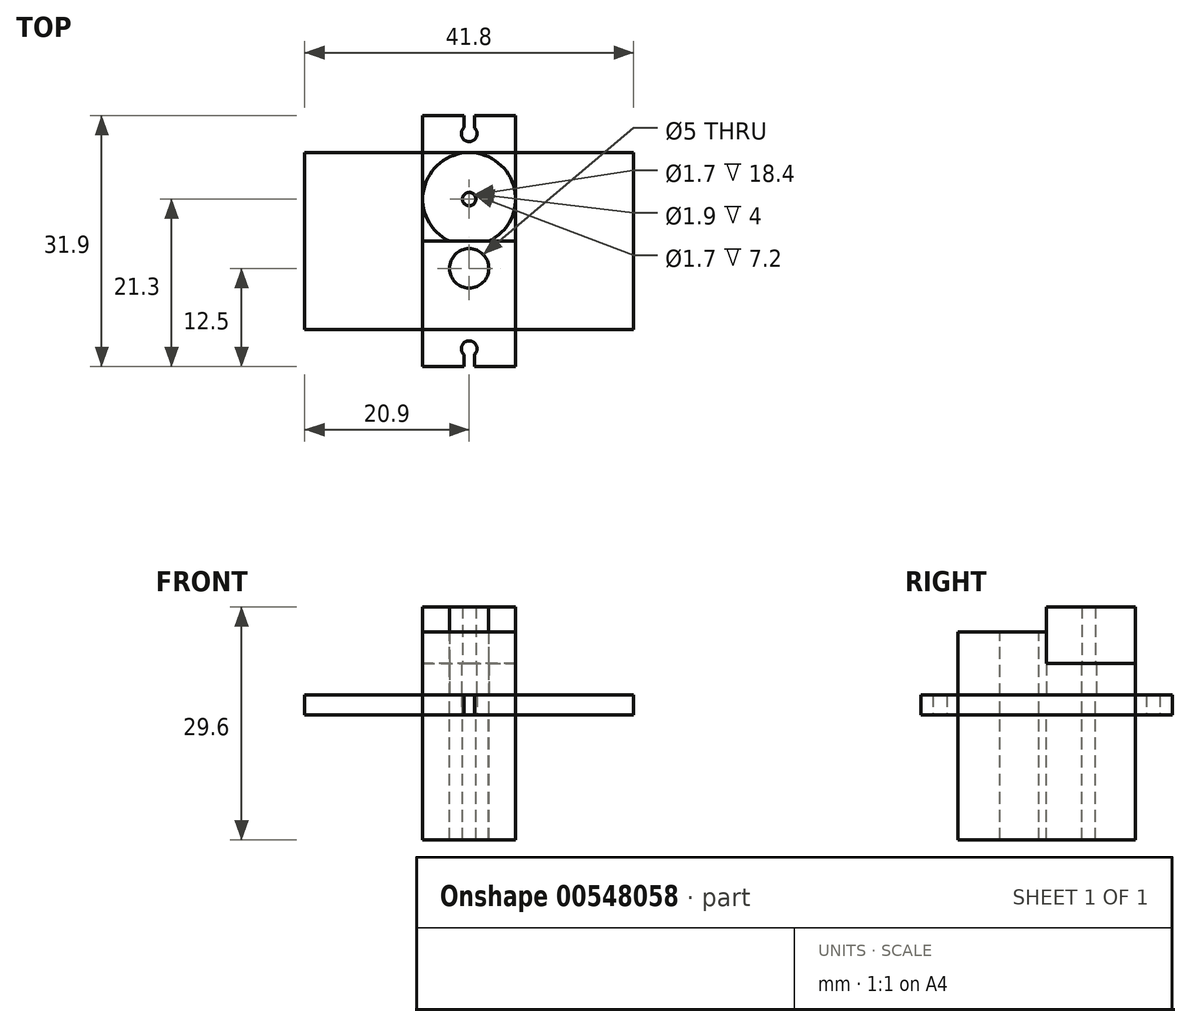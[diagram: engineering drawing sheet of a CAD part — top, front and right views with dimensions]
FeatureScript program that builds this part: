
annotation { "Feature Type Name" : "Feature", "Feature Type Description" : "" }
export const myFeature = defineFeature(function(context is Context, id is Id, definition is map)
    precondition{}
    {
        {
            var Q0;
            Q0=qCreatedBy(makeId("Top.planeOp"),FACE);
            var sketch = newSketch(context, id + "F0", { "sketchPlane" : qUnion([Q0])});
            skLineSegment(sketch, "E0.bottom", {"start": v(0, 0) * mm, "end": v(-11.8, 0) * mm});
            skLineSegment(sketch, "E0.top", {"start": v(0, 31.9) * mm, "end": v(-11.8, 31.9) * mm});
            skLineSegment(sketch, "E0.left", {"start": v(0, 0) * mm, "end": v(0, 31.9) * mm});
            skLineSegment(sketch, "E0.right", {"start": v(-11.8, 0) * mm, "end": v(-11.8, 31.9) * mm});
            skLineSegment(sketch, "E1", {"start": v(-11.8, 27.2) * mm, "end": v(0, 27.2) * mm});
            skLineSegment(sketch, "E2", {"start": v(-11.8, 4.7) * mm, "end": v(0, 4.7) * mm});
            skLineSegment(sketch, "E3", {"start": v(-5.9, 31.9) * mm, "end": v(-5.9, 0) * mm});
            skCircle(sketch, "E4", {"center": v(-5.9, 21.3) * mm, "radius": 5.9 * mm});
            skPoint(sketch, "E4.first.point", {"position": v(-11.8, 21.3) * mm});
            skPoint(sketch, "E4.second.point", {"position": v(0, 21.3) * mm});
            skPoint(sketch, "E4.third.point", {"position": v(-5.9, 27.2) * mm});
            skCircle(sketch, "E5", {"center": v(-5.9, 21.3) * mm, "radius": 2.3 * mm});
            skPoint(sketch, "E6", {"position": v(-6.55, 31.9) * mm});
            skPoint(sketch, "E7", {"position": v(-5.25, 31.9) * mm});
            skPoint(sketch, "E8", {"position": v(-5.9, 29.6) * mm});
            skCircle(sketch, "E9", {"center": v(-5.9, 29.6) * mm, "radius": 1 * mm});
            skLineSegment(sketch, "E10", {"start": v(-6.55, 31.9) * mm, "end": v(-6.55, 30.36) * mm});
            skLineSegment(sketch, "E11", {"start": v(-5.25, 31.9) * mm, "end": v(-5.25, 30.36) * mm});
            skPoint(sketch, "E12", {"position": v(-11.8, 15.95) * mm});
            skPoint(sketch, "E13", {"position": v(0, 15.95) * mm});
            skLineSegment(sketch, "E14", {"start": v(-11.8, 15.95) * mm, "end": v(0, 15.95) * mm});
            skPoint(sketch, "E15.MirrorP", {"position": v(-5.9, 2.3) * mm});
            skLineSegment(sketch, "E16.MirrorCS", {"start": v(-6.55, 0) * mm, "end": v(-6.55, 1.54) * mm});
            skLineSegment(sketch, "E17.MirrorCS", {"start": v(-5.25, 0) * mm, "end": v(-5.25, 1.54) * mm});
            skCircle(sketch, "E18.MirrorC", {"center": v(-5.9, 2.3) * mm, "radius": 1 * mm});
            skCircle(sketch, "E19", {"center": v(-5.9, 21.3) * mm, "radius": 0.85 * mm});
            skPoint(sketch, "E20", {"position": v(-5.9, 12.5) * mm});
            skCircle(sketch, "E21", {"center": v(-5.9, 12.5) * mm, "radius": 2.5 * mm});
            skLineSegment(sketch, "E22", {"start": v(-3.4, 12.5) * mm, "end": v(-3.4, 15.96) * mm});
            skLineSegment(sketch, "E23", {"start": v(-8.4, 12.5) * mm, "end": v(-8.4, 15.96) * mm});
            skSolve(sketch);
        }
        {
            var Q0;
            {var subQ0=sQuery(id+"F0.wireOp",EDGE,"E1");var subQ1=sQuery(id+"F0.wireOp",EDGE,"E0.left");var subQ2=makeQuery(id+"F0.imprint","INTERSECT",VERTEX,{"derivedFrom":[subQ1,subQ0]});Q0=makeQuery(id+"F0.imprint","IMPRINT",FACE,{"disambiguationData":[TD([[makeQuery(id+"F0.imprint","IMPRINT",EDGE,{"disambiguationData":[TD([[subQ2,1.0]])],"derivedFrom":subQ1}),1.0]])]});}
            var Q1;
            {var subQ0=sQuery(id+"F0.wireOp",EDGE,"E1");var subQ1=sQuery(id+"F0.wireOp",EDGE,"E0.right");var subQ2=makeQuery(id+"F0.imprint","INTERSECT",VERTEX,{"derivedFrom":[subQ1,subQ0]});Q1=makeQuery(id+"F0.imprint","IMPRINT",FACE,{"disambiguationData":[TD([[makeQuery(id+"F0.imprint","IMPRINT",EDGE,{"disambiguationData":[TD([[subQ2,1.0]])],"derivedFrom":subQ1}),-1.0]])]});}
            var Q2;
            {var subQ0=sQuery(id+"F0.wireOp",EDGE,"E14");var subQ1=sQuery(id+"F0.wireOp",EDGE,"E0.left");var subQ2=makeQuery(id+"F0.imprint","INTERSECT",VERTEX,{"derivedFrom":[subQ1,subQ0]});Q2=makeQuery(id+"F0.imprint","IMPRINT",FACE,{"disambiguationData":[TD([[makeQuery(id+"F0.imprint","IMPRINT",EDGE,{"disambiguationData":[TD([[subQ2,-1.0]])],"derivedFrom":subQ1}),1.0]])]});}
            var Q3;
            {var subQ0=sQuery(id+"F0.wireOp",EDGE,"E14");var subQ1=sQuery(id+"F0.wireOp",EDGE,"E0.right");var subQ2=makeQuery(id+"F0.imprint","INTERSECT",VERTEX,{"derivedFrom":[subQ1,subQ0]});Q3=makeQuery(id+"F0.imprint","IMPRINT",FACE,{"disambiguationData":[TD([[makeQuery(id+"F0.imprint","IMPRINT",EDGE,{"disambiguationData":[TD([[subQ2,-1.0]])],"derivedFrom":subQ1}),-1.0]])]});}
            var Q4;
            {var subQ1=sQuery(id+"F0.wireOp",EDGE,"E0.left");var subQ6=sQuery(id+"F0.wireOp",EDGE,"E2");var subQ10=makeQuery(id+"F0.imprint","INTERSECT",VERTEX,{"derivedFrom":[subQ1,subQ6]});Q4=makeQuery(id+"F0.imprint","IMPRINT",FACE,{"disambiguationData":[TD([[makeQuery(id+"F0.imprint","IMPRINT",EDGE,{"disambiguationData":[TD([[subQ10,-1.0]])],"derivedFrom":subQ1}),1.0]])]});}
            var Q5;
            {var subQ1=sQuery(id+"F0.wireOp",EDGE,"E0.right");var subQ5=sQuery(id+"F0.wireOp",EDGE,"E2");var subQ6=makeQuery(id+"F0.imprint","INTERSECT",VERTEX,{"derivedFrom":[subQ1,subQ5]});Q5=makeQuery(id+"F0.imprint","IMPRINT",FACE,{"disambiguationData":[TD([[makeQuery(id+"F0.imprint","IMPRINT",EDGE,{"disambiguationData":[TD([[subQ6,-1.0]])],"derivedFrom":subQ1}),-1.0]])]});}
            var Q6;
            {var subQ5=sQuery(id+"F0.wireOp",EDGE,"E3");var subQ7=sQuery(id+"F0.wireOp",EDGE,"E5");var subQ8=makeQuery(id+"F0.imprint","INTERSECT",VERTEX,{"disambiguationData":[OD(1.0)],"derivedFrom":[subQ5,subQ7]});Q6=makeQuery(id+"F0.imprint","IMPRINT",FACE,{"disambiguationData":[TD([[makeQuery(id+"F0.imprint","IMPRINT",EDGE,{"disambiguationData":[TD([[subQ8,-1.0]])],"derivedFrom":subQ5}),1.0]])]});}
            var Q7;
            {var subQ0=sQuery(id+"F0.wireOp",EDGE,"E5");var subQ1=sQuery(id+"F0.wireOp",EDGE,"E3");var subQ2=makeQuery(id+"F0.imprint","INTERSECT",VERTEX,{"disambiguationData":[OD(0.0)],"derivedFrom":[subQ1,subQ0]});Q7=makeQuery(id+"F0.imprint","IMPRINT",FACE,{"disambiguationData":[TD([[makeQuery(id+"F0.imprint","IMPRINT",EDGE,{"disambiguationData":[TD([[subQ2,-1.0]])],"derivedFrom":subQ1}),1.0]])]});}
            var Q8;
            {var subQ0=sQuery(id+"F0.wireOp",EDGE,"E5");var subQ1=sQuery(id+"F0.wireOp",EDGE,"E3");var subQ2=makeQuery(id+"F0.imprint","INTERSECT",VERTEX,{"disambiguationData":[OD(0.0)],"derivedFrom":[subQ1,subQ0]});Q8=makeQuery(id+"F0.imprint","IMPRINT",FACE,{"disambiguationData":[TD([[makeQuery(id+"F0.imprint","IMPRINT",EDGE,{"disambiguationData":[TD([[subQ2,-1.0]])],"derivedFrom":subQ1}),-1.0]])]});}
            var Q9;
            {var subQ0=sQuery(id+"F0.wireOp",EDGE,"E19");var subQ1=sQuery(id+"F0.wireOp",EDGE,"E3");var subQ2=makeQuery(id+"F0.imprint","INTERSECT",VERTEX,{"disambiguationData":[OD(0.0)],"derivedFrom":[subQ1,subQ0]});Q9=makeQuery(id+"F0.imprint","IMPRINT",FACE,{"disambiguationData":[TD([[makeQuery(id+"F0.imprint","IMPRINT",EDGE,{"disambiguationData":[TD([[subQ2,-1.0]])],"derivedFrom":subQ1}),1.0]])]});}
            var Q10;
            {var subQ0=sQuery(id+"F0.wireOp",EDGE,"E19");var subQ1=sQuery(id+"F0.wireOp",EDGE,"E3");var subQ2=makeQuery(id+"F0.imprint","INTERSECT",VERTEX,{"disambiguationData":[OD(0.0)],"derivedFrom":[subQ1,subQ0]});Q10=makeQuery(id+"F0.imprint","IMPRINT",FACE,{"disambiguationData":[TD([[makeQuery(id+"F0.imprint","IMPRINT",EDGE,{"disambiguationData":[TD([[subQ2,-1.0]])],"derivedFrom":subQ1}),-1.0]])]});}
            var Q11;
            {var subQ0=sQuery(id+"F0.wireOp",EDGE,"E21");var subQ1=sQuery(id+"F0.wireOp",EDGE,"E3");var subQ2=makeQuery(id+"F0.imprint","INTERSECT",VERTEX,{"disambiguationData":[OD(0.0)],"derivedFrom":[subQ1,subQ0]});Q11=makeQuery(id+"F0.imprint","IMPRINT",FACE,{"disambiguationData":[TD([[makeQuery(id+"F0.imprint","IMPRINT",EDGE,{"disambiguationData":[TD([[subQ2,-1.0]])],"derivedFrom":subQ1}),-1.0]])]});}
            var Q12;
            {var subQ0=sQuery(id+"F0.wireOp",EDGE,"E21");var subQ1=sQuery(id+"F0.wireOp",EDGE,"E3");var subQ2=makeQuery(id+"F0.imprint","INTERSECT",VERTEX,{"disambiguationData":[OD(0.0)],"derivedFrom":[subQ1,subQ0]});Q12=makeQuery(id+"F0.imprint","IMPRINT",FACE,{"disambiguationData":[TD([[makeQuery(id+"F0.imprint","IMPRINT",EDGE,{"disambiguationData":[TD([[subQ2,-1.0]])],"derivedFrom":subQ1}),1.0]])]});}
            var Q13;
            {var subQ3=sQuery(id+"F0.wireOp",EDGE,"E3");var subQ6=sQuery(id+"F0.wireOp",EDGE,"E4");var subQ9=makeQuery(id+"F0.imprint","INTERSECT",VERTEX,{"derivedFrom":[subQ3,subQ6]});Q13=makeQuery(id+"F0.imprint","IMPRINT",FACE,{"disambiguationData":[TD([[makeQuery(id+"F0.imprint","IMPRINT",EDGE,{"disambiguationData":[TD([[subQ9,-1.0]])],"derivedFrom":subQ3}),1.0]])]});}
            var Q14;
            {var subQ0=sQuery(id+"F0.wireOp",EDGE,"E14");var subQ1=sQuery(id+"F0.wireOp",EDGE,"E3");var subQ2=makeQuery(id+"F0.imprint","INTERSECT",VERTEX,{"derivedFrom":[subQ1,subQ0]});Q14=makeQuery(id+"F0.imprint","IMPRINT",FACE,{"disambiguationData":[TD([[makeQuery(id+"F0.imprint","IMPRINT",EDGE,{"disambiguationData":[TD([[subQ2,-1.0]])],"derivedFrom":subQ1}),1.0]])]});}
            var Q15;
            {var subQ3=sQuery(id+"F0.wireOp",EDGE,"E3");var subQ6=sQuery(id+"F0.wireOp",EDGE,"E4");var subQ9=makeQuery(id+"F0.imprint","INTERSECT",VERTEX,{"derivedFrom":[subQ3,subQ6]});Q15=makeQuery(id+"F0.imprint","IMPRINT",FACE,{"disambiguationData":[TD([[makeQuery(id+"F0.imprint","IMPRINT",EDGE,{"disambiguationData":[TD([[subQ9,-1.0]])],"derivedFrom":subQ3}),-1.0]])]});}
            var Q16;
            {var subQ2=sQuery(id+"F0.wireOp",EDGE,"E3");var subQ5=sQuery(id+"F0.wireOp",EDGE,"E5");var subQ6=makeQuery(id+"F0.imprint","INTERSECT",VERTEX,{"disambiguationData":[OD(1.0)],"derivedFrom":[subQ2,subQ5]});Q16=makeQuery(id+"F0.imprint","IMPRINT",FACE,{"disambiguationData":[TD([[makeQuery(id+"F0.imprint","IMPRINT",EDGE,{"disambiguationData":[TD([[subQ6,-1.0]])],"derivedFrom":subQ2}),-1.0]])]});}
            var Q17;
            {var subQ0=sQuery(id+"F0.wireOp",EDGE,"E14");var subQ1=sQuery(id+"F0.wireOp",EDGE,"E3");var subQ2=makeQuery(id+"F0.imprint","INTERSECT",VERTEX,{"derivedFrom":[subQ1,subQ0]});Q17=makeQuery(id+"F0.imprint","IMPRINT",FACE,{"disambiguationData":[TD([[makeQuery(id+"F0.imprint","IMPRINT",EDGE,{"disambiguationData":[TD([[subQ2,-1.0]])],"derivedFrom":subQ1}),-1.0]])]});}
            extrude(context, id + "F1", {"entities" : qUnion([Q0, Q1, Q2, Q3, Q4, Q5, Q6, Q7, Q8, Q9, Q10, Q11, Q12, Q13, Q14, Q15, Q16, Q17]), "oppositeDirection" : true, "depth" : 15.9 * mm});
        }
        {
            var Q0;
            {var subQ0=sQuery(id+"F0.wireOp",EDGE,"E1");var subQ1=sQuery(id+"F0.wireOp",EDGE,"E0.left");var subQ2=makeQuery(id+"F0.imprint","INTERSECT",VERTEX,{"derivedFrom":[subQ1,subQ0]});Q0=makeQuery(id+"F0.imprint","IMPRINT",FACE,{"disambiguationData":[TD([[makeQuery(id+"F0.imprint","IMPRINT",EDGE,{"disambiguationData":[TD([[subQ2,1.0]])],"derivedFrom":subQ1}),1.0]])]});}
            var Q1;
            {var subQ0=sQuery(id+"F0.wireOp",EDGE,"E1");var subQ1=sQuery(id+"F0.wireOp",EDGE,"E0.right");var subQ2=makeQuery(id+"F0.imprint","INTERSECT",VERTEX,{"derivedFrom":[subQ1,subQ0]});Q1=makeQuery(id+"F0.imprint","IMPRINT",FACE,{"disambiguationData":[TD([[makeQuery(id+"F0.imprint","IMPRINT",EDGE,{"disambiguationData":[TD([[subQ2,1.0]])],"derivedFrom":subQ1}),-1.0]])]});}
            var Q2;
            {var subQ0=sQuery(id+"F0.wireOp",EDGE,"E14");var subQ1=sQuery(id+"F0.wireOp",EDGE,"E0.left");var subQ2=makeQuery(id+"F0.imprint","INTERSECT",VERTEX,{"derivedFrom":[subQ1,subQ0]});Q2=makeQuery(id+"F0.imprint","IMPRINT",FACE,{"disambiguationData":[TD([[makeQuery(id+"F0.imprint","IMPRINT",EDGE,{"disambiguationData":[TD([[subQ2,-1.0]])],"derivedFrom":subQ1}),1.0]])]});}
            var Q3;
            {var subQ0=sQuery(id+"F0.wireOp",EDGE,"E14");var subQ1=sQuery(id+"F0.wireOp",EDGE,"E0.right");var subQ2=makeQuery(id+"F0.imprint","INTERSECT",VERTEX,{"derivedFrom":[subQ1,subQ0]});Q3=makeQuery(id+"F0.imprint","IMPRINT",FACE,{"disambiguationData":[TD([[makeQuery(id+"F0.imprint","IMPRINT",EDGE,{"disambiguationData":[TD([[subQ2,-1.0]])],"derivedFrom":subQ1}),-1.0]])]});}
            var Q4;
            {var subQ9=sQuery(id+"F0.wireOp",EDGE,"E17.MirrorCS");Q4=makeQuery(id+"F0.imprint","IMPRINT",FACE,{"disambiguationData":[TD([[makeQuery(id+"F0.imprint","IMPRINT",EDGE,{"derivedFrom":subQ9}),-1.0]])]});}
            var Q5;
            {var subQ9=sQuery(id+"F0.wireOp",EDGE,"E16.MirrorCS");Q5=makeQuery(id+"F0.imprint","IMPRINT",FACE,{"disambiguationData":[TD([[makeQuery(id+"F0.imprint","IMPRINT",EDGE,{"derivedFrom":subQ9}),1.0]])]});}
            var Q6;
            {var subQ9=sQuery(id+"F0.wireOp",EDGE,"E11");Q6=makeQuery(id+"F0.imprint","IMPRINT",FACE,{"disambiguationData":[TD([[makeQuery(id+"F0.imprint","IMPRINT",EDGE,{"derivedFrom":subQ9}),1.0]])]});}
            var Q7;
            {var subQ9=sQuery(id+"F0.wireOp",EDGE,"E10");Q7=makeQuery(id+"F0.imprint","IMPRINT",FACE,{"disambiguationData":[TD([[makeQuery(id+"F0.imprint","IMPRINT",EDGE,{"derivedFrom":subQ9}),-1.0]])]});}
            var Q8;
            {var subQ1=sQuery(id+"F0.wireOp",EDGE,"E0.left");var subQ6=sQuery(id+"F0.wireOp",EDGE,"E2");var subQ10=makeQuery(id+"F0.imprint","INTERSECT",VERTEX,{"derivedFrom":[subQ1,subQ6]});Q8=makeQuery(id+"F0.imprint","IMPRINT",FACE,{"disambiguationData":[TD([[makeQuery(id+"F0.imprint","IMPRINT",EDGE,{"disambiguationData":[TD([[subQ10,-1.0]])],"derivedFrom":subQ1}),1.0]])]});}
            var Q9;
            {var subQ1=sQuery(id+"F0.wireOp",EDGE,"E0.right");var subQ5=sQuery(id+"F0.wireOp",EDGE,"E2");var subQ6=makeQuery(id+"F0.imprint","INTERSECT",VERTEX,{"derivedFrom":[subQ1,subQ5]});Q9=makeQuery(id+"F0.imprint","IMPRINT",FACE,{"disambiguationData":[TD([[makeQuery(id+"F0.imprint","IMPRINT",EDGE,{"disambiguationData":[TD([[subQ6,-1.0]])],"derivedFrom":subQ1}),-1.0]])]});}
            var Q10;
            {var subQ5=sQuery(id+"F0.wireOp",EDGE,"E3");var subQ7=sQuery(id+"F0.wireOp",EDGE,"E5");var subQ8=makeQuery(id+"F0.imprint","INTERSECT",VERTEX,{"disambiguationData":[OD(1.0)],"derivedFrom":[subQ5,subQ7]});Q10=makeQuery(id+"F0.imprint","IMPRINT",FACE,{"disambiguationData":[TD([[makeQuery(id+"F0.imprint","IMPRINT",EDGE,{"disambiguationData":[TD([[subQ8,-1.0]])],"derivedFrom":subQ5}),1.0]])]});}
            var Q11;
            {var subQ2=sQuery(id+"F0.wireOp",EDGE,"E3");var subQ5=sQuery(id+"F0.wireOp",EDGE,"E5");var subQ6=makeQuery(id+"F0.imprint","INTERSECT",VERTEX,{"disambiguationData":[OD(1.0)],"derivedFrom":[subQ2,subQ5]});Q11=makeQuery(id+"F0.imprint","IMPRINT",FACE,{"disambiguationData":[TD([[makeQuery(id+"F0.imprint","IMPRINT",EDGE,{"disambiguationData":[TD([[subQ6,-1.0]])],"derivedFrom":subQ2}),-1.0]])]});}
            var Q12;
            {var subQ0=sQuery(id+"F0.wireOp",EDGE,"E14");var subQ1=sQuery(id+"F0.wireOp",EDGE,"E3");var subQ2=makeQuery(id+"F0.imprint","INTERSECT",VERTEX,{"derivedFrom":[subQ1,subQ0]});Q12=makeQuery(id+"F0.imprint","IMPRINT",FACE,{"disambiguationData":[TD([[makeQuery(id+"F0.imprint","IMPRINT",EDGE,{"disambiguationData":[TD([[subQ2,-1.0]])],"derivedFrom":subQ1}),1.0]])]});}
            var Q13;
            {var subQ0=sQuery(id+"F0.wireOp",EDGE,"E14");var subQ1=sQuery(id+"F0.wireOp",EDGE,"E3");var subQ2=makeQuery(id+"F0.imprint","INTERSECT",VERTEX,{"derivedFrom":[subQ1,subQ0]});Q13=makeQuery(id+"F0.imprint","IMPRINT",FACE,{"disambiguationData":[TD([[makeQuery(id+"F0.imprint","IMPRINT",EDGE,{"disambiguationData":[TD([[subQ2,-1.0]])],"derivedFrom":subQ1}),-1.0]])]});}
            var Q14;
            {var subQ0=sQuery(id+"F0.wireOp",EDGE,"E21");var subQ1=sQuery(id+"F0.wireOp",EDGE,"E3");var subQ2=makeQuery(id+"F0.imprint","INTERSECT",VERTEX,{"disambiguationData":[OD(0.0)],"derivedFrom":[subQ1,subQ0]});Q14=makeQuery(id+"F0.imprint","IMPRINT",FACE,{"disambiguationData":[TD([[makeQuery(id+"F0.imprint","IMPRINT",EDGE,{"disambiguationData":[TD([[subQ2,-1.0]])],"derivedFrom":subQ1}),1.0]])]});}
            var Q15;
            {var subQ0=sQuery(id+"F0.wireOp",EDGE,"E5");var subQ1=sQuery(id+"F0.wireOp",EDGE,"E3");var subQ2=makeQuery(id+"F0.imprint","INTERSECT",VERTEX,{"disambiguationData":[OD(0.0)],"derivedFrom":[subQ1,subQ0]});Q15=makeQuery(id+"F0.imprint","IMPRINT",FACE,{"disambiguationData":[TD([[makeQuery(id+"F0.imprint","IMPRINT",EDGE,{"disambiguationData":[TD([[subQ2,-1.0]])],"derivedFrom":subQ1}),-1.0]])]});}
            var Q16;
            {var subQ3=sQuery(id+"F0.wireOp",EDGE,"E3");var subQ6=sQuery(id+"F0.wireOp",EDGE,"E4");var subQ9=makeQuery(id+"F0.imprint","INTERSECT",VERTEX,{"derivedFrom":[subQ3,subQ6]});Q16=makeQuery(id+"F0.imprint","IMPRINT",FACE,{"disambiguationData":[TD([[makeQuery(id+"F0.imprint","IMPRINT",EDGE,{"disambiguationData":[TD([[subQ9,-1.0]])],"derivedFrom":subQ3}),1.0]])]});}
            var Q17;
            {var subQ0=sQuery(id+"F0.wireOp",EDGE,"E5");var subQ1=sQuery(id+"F0.wireOp",EDGE,"E3");var subQ2=makeQuery(id+"F0.imprint","INTERSECT",VERTEX,{"disambiguationData":[OD(0.0)],"derivedFrom":[subQ1,subQ0]});Q17=makeQuery(id+"F0.imprint","IMPRINT",FACE,{"disambiguationData":[TD([[makeQuery(id+"F0.imprint","IMPRINT",EDGE,{"disambiguationData":[TD([[subQ2,-1.0]])],"derivedFrom":subQ1}),1.0]])]});}
            var Q18;
            {var subQ0=sQuery(id+"F0.wireOp",EDGE,"E21");var subQ1=sQuery(id+"F0.wireOp",EDGE,"E3");var subQ2=makeQuery(id+"F0.imprint","INTERSECT",VERTEX,{"disambiguationData":[OD(0.0)],"derivedFrom":[subQ1,subQ0]});Q18=makeQuery(id+"F0.imprint","IMPRINT",FACE,{"disambiguationData":[TD([[makeQuery(id+"F0.imprint","IMPRINT",EDGE,{"disambiguationData":[TD([[subQ2,-1.0]])],"derivedFrom":subQ1}),-1.0]])]});}
            var Q19;
            {var subQ3=sQuery(id+"F0.wireOp",EDGE,"E3");var subQ6=sQuery(id+"F0.wireOp",EDGE,"E4");var subQ9=makeQuery(id+"F0.imprint","INTERSECT",VERTEX,{"derivedFrom":[subQ3,subQ6]});Q19=makeQuery(id+"F0.imprint","IMPRINT",FACE,{"disambiguationData":[TD([[makeQuery(id+"F0.imprint","IMPRINT",EDGE,{"disambiguationData":[TD([[subQ9,-1.0]])],"derivedFrom":subQ3}),-1.0]])]});}
            var Q20;
            {var subQ0=sQuery(id+"F0.wireOp",EDGE,"E23");var subQ1=sQuery(id+"F0.wireOp",EDGE,"E4");var subQ2=makeQuery(id+"F0.imprint","INTERSECT",VERTEX,{"derivedFrom":[subQ1,subQ0]});Q20=makeQuery(id+"F0.imprint","IMPRINT",FACE,{"disambiguationData":[TD([[makeQuery(id+"F0.imprint","IMPRINT",EDGE,{"disambiguationData":[TD([[subQ2,-1.0]])],"derivedFrom":subQ1}),-1.0]])]});}
            var Q21;
            {var subQ0=sQuery(id+"F0.wireOp",EDGE,"E22");var subQ1=sQuery(id+"F0.wireOp",EDGE,"E4");var subQ2=makeQuery(id+"F0.imprint","INTERSECT",VERTEX,{"derivedFrom":[subQ1,subQ0]});Q21=makeQuery(id+"F0.imprint","IMPRINT",FACE,{"disambiguationData":[TD([[makeQuery(id+"F0.imprint","IMPRINT",EDGE,{"disambiguationData":[TD([[subQ2,1.0]])],"derivedFrom":subQ1}),-1.0]])]});}
            var Q22;
            {var subQ0=sQuery(id+"F0.wireOp",EDGE,"E19");var subQ1=sQuery(id+"F0.wireOp",EDGE,"E3");var subQ2=makeQuery(id+"F0.imprint","INTERSECT",VERTEX,{"disambiguationData":[OD(0.0)],"derivedFrom":[subQ1,subQ0]});Q22=makeQuery(id+"F0.imprint","IMPRINT",FACE,{"disambiguationData":[TD([[makeQuery(id+"F0.imprint","IMPRINT",EDGE,{"disambiguationData":[TD([[subQ2,-1.0]])],"derivedFrom":subQ1}),1.0]])]});}
            var Q23;
            {var subQ0=sQuery(id+"F0.wireOp",EDGE,"E19");var subQ1=sQuery(id+"F0.wireOp",EDGE,"E3");var subQ2=makeQuery(id+"F0.imprint","INTERSECT",VERTEX,{"disambiguationData":[OD(0.0)],"derivedFrom":[subQ1,subQ0]});Q23=makeQuery(id+"F0.imprint","IMPRINT",FACE,{"disambiguationData":[TD([[makeQuery(id+"F0.imprint","IMPRINT",EDGE,{"disambiguationData":[TD([[subQ2,-1.0]])],"derivedFrom":subQ1}),-1.0]])]});}
            extrude(context, id + "F2", {"entities" : qUnion([Q0, Q1, Q2, Q3, Q4, Q5, Q6, Q7, Q8, Q9, Q10, Q11, Q12, Q13, Q14, Q15, Q16, Q17, Q18, Q19, Q20, Q21, Q22, Q23]), "operationType" : NewBodyOperationType.ADD, "depth" : 2.5 * mm});
        }
        {
            var Q0;
            Q0=makeQuery(id+"F2.opExtrude","CAP_EDGE",EDGE,{"disambiguationData":[OSD([sQuery(id+"F0.wireOp",EDGE,"E0.right")])],"isStart":false});
            cPlane(context, id + "F3", {"entities" : qUnion([Q0]), "cplaneType" : CPlaneType.LINE_ANGLE, "offset" : 25 * mm, "angle" : 0 * degree, "width" : 150 * mm, "height" : 150 * mm});
        }
        {
            var Q0;
            Q0=qCreatedBy(id+"F3.planeOp",FACE);
            var sketch = newSketch(context, id + "F4", { "sketchPlane" : qUnion([Q0])});
            skLineSegment(sketch, "E24.bottom", {"start": v(0, 0) * mm, "end": v(-11.8, 0) * mm});
            skLineSegment(sketch, "E24.top", {"start": v(0, 31.9) * mm, "end": v(-11.8, 31.9) * mm});
            skLineSegment(sketch, "E24.left", {"start": v(0, 0) * mm, "end": v(0, 31.9) * mm});
            skLineSegment(sketch, "E24.right", {"start": v(-11.8, 0) * mm, "end": v(-11.8, 31.9) * mm});
            skLineSegment(sketch, "E25", {"start": v(-11.8, 27.2) * mm, "end": v(0, 27.2) * mm});
            skLineSegment(sketch, "E26", {"start": v(-11.8, 4.7) * mm, "end": v(0, 4.7) * mm});
            skLineSegment(sketch, "E27", {"start": v(-5.9, 31.9) * mm, "end": v(-5.9, 0) * mm});
            skCircle(sketch, "E28", {"center": v(-5.9, 21.3) * mm, "radius": 5.9 * mm});
            skPoint(sketch, "E28.first.point", {"position": v(-11.8, 21.3) * mm});
            skPoint(sketch, "E28.second.point", {"position": v(0, 21.3) * mm});
            skPoint(sketch, "E28.third.point", {"position": v(-5.9, 27.2) * mm});
            skCircle(sketch, "E29", {"center": v(-5.9, 21.3) * mm, "radius": 2.3 * mm});
            skPoint(sketch, "E30", {"position": v(-6.55, 31.9) * mm});
            skPoint(sketch, "E31", {"position": v(-5.25, 31.9) * mm});
            skPoint(sketch, "E32", {"position": v(-5.9, 29.6) * mm});
            skCircle(sketch, "E33", {"center": v(-5.9, 29.6) * mm, "radius": 1 * mm});
            skLineSegment(sketch, "E34", {"start": v(-6.55, 31.9) * mm, "end": v(-6.55, 30.36) * mm});
            skLineSegment(sketch, "E35", {"start": v(-5.25, 31.9) * mm, "end": v(-5.25, 30.36) * mm});
            skPoint(sketch, "E36", {"position": v(-11.8, 15.95) * mm});
            skPoint(sketch, "E37", {"position": v(0, 15.95) * mm});
            skLineSegment(sketch, "E38", {"start": v(-11.8, 15.95) * mm, "end": v(0, 15.95) * mm});
            skPoint(sketch, "E39.MirrorP", {"position": v(-5.9, 2.3) * mm});
            skLineSegment(sketch, "E40.MirrorCS", {"start": v(-6.55, 0) * mm, "end": v(-6.55, 1.54) * mm});
            skLineSegment(sketch, "E41.MirrorCS", {"start": v(-5.25, 0) * mm, "end": v(-5.25, 1.54) * mm});
            skCircle(sketch, "E42.MirrorC", {"center": v(-5.9, 2.3) * mm, "radius": 1 * mm});
            skCircle(sketch, "E43", {"center": v(-5.9, 21.3) * mm, "radius": 0.95 * mm});
            skPoint(sketch, "E44", {"position": v(-5.9, 12.5) * mm});
            skCircle(sketch, "E45", {"center": v(-5.9, 12.5) * mm, "radius": 2.5 * mm});
            skLineSegment(sketch, "E46", {"start": v(-3.4, 12.5) * mm, "end": v(-3.4, 15.96) * mm});
            skLineSegment(sketch, "E47", {"start": v(-8.4, 12.5) * mm, "end": v(-8.4, 15.96) * mm});
            skSolve(sketch);
        }
        {
            var Q0;
            {var subQ0=sQuery(id+"F4.wireOp",EDGE,"E25");var subQ1=sQuery(id+"F4.wireOp",EDGE,"E24.left");var subQ2=makeQuery(id+"F4.imprint","INTERSECT",VERTEX,{"derivedFrom":[subQ1,subQ0]});Q0=makeQuery(id+"F4.imprint","IMPRINT",FACE,{"disambiguationData":[TD([[makeQuery(id+"F4.imprint","IMPRINT",EDGE,{"disambiguationData":[TD([[subQ2,1.0]])],"derivedFrom":subQ1}),1.0]])]});}
            var Q1;
            {var subQ0=sQuery(id+"F4.wireOp",EDGE,"E25");var subQ1=sQuery(id+"F4.wireOp",EDGE,"E24.right");var subQ2=makeQuery(id+"F4.imprint","INTERSECT",VERTEX,{"derivedFrom":[subQ1,subQ0]});Q1=makeQuery(id+"F4.imprint","IMPRINT",FACE,{"disambiguationData":[TD([[makeQuery(id+"F4.imprint","IMPRINT",EDGE,{"disambiguationData":[TD([[subQ2,1.0]])],"derivedFrom":subQ1}),-1.0]])]});}
            var Q2;
            {var subQ0=sQuery(id+"F4.wireOp",EDGE,"E38");var subQ1=sQuery(id+"F4.wireOp",EDGE,"E24.left");var subQ2=makeQuery(id+"F4.imprint","INTERSECT",VERTEX,{"derivedFrom":[subQ1,subQ0]});Q2=makeQuery(id+"F4.imprint","IMPRINT",FACE,{"disambiguationData":[TD([[makeQuery(id+"F4.imprint","IMPRINT",EDGE,{"disambiguationData":[TD([[subQ2,-1.0]])],"derivedFrom":subQ1}),1.0]])]});}
            var Q3;
            {var subQ0=sQuery(id+"F4.wireOp",EDGE,"E38");var subQ1=sQuery(id+"F4.wireOp",EDGE,"E24.right");var subQ2=makeQuery(id+"F4.imprint","INTERSECT",VERTEX,{"derivedFrom":[subQ1,subQ0]});Q3=makeQuery(id+"F4.imprint","IMPRINT",FACE,{"disambiguationData":[TD([[makeQuery(id+"F4.imprint","IMPRINT",EDGE,{"disambiguationData":[TD([[subQ2,-1.0]])],"derivedFrom":subQ1}),-1.0]])]});}
            var Q4;
            {var subQ1=sQuery(id+"F4.wireOp",EDGE,"E24.left");var subQ6=sQuery(id+"F4.wireOp",EDGE,"E26");var subQ10=makeQuery(id+"F4.imprint","INTERSECT",VERTEX,{"derivedFrom":[subQ1,subQ6]});Q4=makeQuery(id+"F4.imprint","IMPRINT",FACE,{"disambiguationData":[TD([[makeQuery(id+"F4.imprint","IMPRINT",EDGE,{"disambiguationData":[TD([[subQ10,-1.0]])],"derivedFrom":subQ1}),1.0]])]});}
            var Q5;
            {var subQ1=sQuery(id+"F4.wireOp",EDGE,"E24.right");var subQ5=sQuery(id+"F4.wireOp",EDGE,"E26");var subQ6=makeQuery(id+"F4.imprint","INTERSECT",VERTEX,{"derivedFrom":[subQ1,subQ5]});Q5=makeQuery(id+"F4.imprint","IMPRINT",FACE,{"disambiguationData":[TD([[makeQuery(id+"F4.imprint","IMPRINT",EDGE,{"disambiguationData":[TD([[subQ6,-1.0]])],"derivedFrom":subQ1}),-1.0]])]});}
            var Q6;
            {var subQ5=sQuery(id+"F4.wireOp",EDGE,"E27");var subQ7=sQuery(id+"F4.wireOp",EDGE,"E29");var subQ8=makeQuery(id+"F4.imprint","INTERSECT",VERTEX,{"disambiguationData":[OD(1.0)],"derivedFrom":[subQ5,subQ7]});Q6=makeQuery(id+"F4.imprint","IMPRINT",FACE,{"disambiguationData":[TD([[makeQuery(id+"F4.imprint","IMPRINT",EDGE,{"disambiguationData":[TD([[subQ8,-1.0]])],"derivedFrom":subQ5}),1.0]])]});}
            var Q7;
            {var subQ2=sQuery(id+"F4.wireOp",EDGE,"E27");var subQ5=sQuery(id+"F4.wireOp",EDGE,"E29");var subQ6=makeQuery(id+"F4.imprint","INTERSECT",VERTEX,{"disambiguationData":[OD(1.0)],"derivedFrom":[subQ2,subQ5]});Q7=makeQuery(id+"F4.imprint","IMPRINT",FACE,{"disambiguationData":[TD([[makeQuery(id+"F4.imprint","IMPRINT",EDGE,{"disambiguationData":[TD([[subQ6,-1.0]])],"derivedFrom":subQ2}),-1.0]])]});}
            var Q8;
            {var subQ0=sQuery(id+"F4.wireOp",EDGE,"E45");var subQ1=sQuery(id+"F4.wireOp",EDGE,"E27");var subQ2=makeQuery(id+"F4.imprint","INTERSECT",VERTEX,{"disambiguationData":[OD(0.0)],"derivedFrom":[subQ1,subQ0]});Q8=makeQuery(id+"F4.imprint","IMPRINT",FACE,{"disambiguationData":[TD([[makeQuery(id+"F4.imprint","IMPRINT",EDGE,{"disambiguationData":[TD([[subQ2,-1.0]])],"derivedFrom":subQ1}),1.0]])]});}
            var Q9;
            {var subQ0=sQuery(id+"F4.wireOp",EDGE,"E45");var subQ1=sQuery(id+"F4.wireOp",EDGE,"E27");var subQ2=makeQuery(id+"F4.imprint","INTERSECT",VERTEX,{"disambiguationData":[OD(0.0)],"derivedFrom":[subQ1,subQ0]});Q9=makeQuery(id+"F4.imprint","IMPRINT",FACE,{"disambiguationData":[TD([[makeQuery(id+"F4.imprint","IMPRINT",EDGE,{"disambiguationData":[TD([[subQ2,-1.0]])],"derivedFrom":subQ1}),-1.0]])]});}
            var Q10;
            {var subQ3=sQuery(id+"F4.wireOp",EDGE,"E27");var subQ6=sQuery(id+"F4.wireOp",EDGE,"E28");var subQ9=makeQuery(id+"F4.imprint","INTERSECT",VERTEX,{"derivedFrom":[subQ3,subQ6]});Q10=makeQuery(id+"F4.imprint","IMPRINT",FACE,{"disambiguationData":[TD([[makeQuery(id+"F4.imprint","IMPRINT",EDGE,{"disambiguationData":[TD([[subQ9,-1.0]])],"derivedFrom":subQ3}),-1.0]])]});}
            var Q11;
            {var subQ3=sQuery(id+"F4.wireOp",EDGE,"E27");var subQ6=sQuery(id+"F4.wireOp",EDGE,"E28");var subQ9=makeQuery(id+"F4.imprint","INTERSECT",VERTEX,{"derivedFrom":[subQ3,subQ6]});Q11=makeQuery(id+"F4.imprint","IMPRINT",FACE,{"disambiguationData":[TD([[makeQuery(id+"F4.imprint","IMPRINT",EDGE,{"disambiguationData":[TD([[subQ9,-1.0]])],"derivedFrom":subQ3}),1.0]])]});}
            var Q12;
            {var subQ0=sQuery(id+"F4.wireOp",EDGE,"E38");var subQ1=sQuery(id+"F4.wireOp",EDGE,"E27");var subQ2=makeQuery(id+"F4.imprint","INTERSECT",VERTEX,{"derivedFrom":[subQ1,subQ0]});Q12=makeQuery(id+"F4.imprint","IMPRINT",FACE,{"disambiguationData":[TD([[makeQuery(id+"F4.imprint","IMPRINT",EDGE,{"disambiguationData":[TD([[subQ2,-1.0]])],"derivedFrom":subQ1}),1.0]])]});}
            var Q13;
            {var subQ0=sQuery(id+"F4.wireOp",EDGE,"E38");var subQ1=sQuery(id+"F4.wireOp",EDGE,"E27");var subQ2=makeQuery(id+"F4.imprint","INTERSECT",VERTEX,{"derivedFrom":[subQ1,subQ0]});Q13=makeQuery(id+"F4.imprint","IMPRINT",FACE,{"disambiguationData":[TD([[makeQuery(id+"F4.imprint","IMPRINT",EDGE,{"disambiguationData":[TD([[subQ2,-1.0]])],"derivedFrom":subQ1}),-1.0]])]});}
            var Q14;
            {var subQ0=sQuery(id+"F4.wireOp",EDGE,"E29");var subQ1=sQuery(id+"F4.wireOp",EDGE,"E27");var subQ2=makeQuery(id+"F4.imprint","INTERSECT",VERTEX,{"disambiguationData":[OD(0.0)],"derivedFrom":[subQ1,subQ0]});Q14=makeQuery(id+"F4.imprint","IMPRINT",FACE,{"disambiguationData":[TD([[makeQuery(id+"F4.imprint","IMPRINT",EDGE,{"disambiguationData":[TD([[subQ2,-1.0]])],"derivedFrom":subQ1}),-1.0]])]});}
            var Q15;
            {var subQ0=sQuery(id+"F4.wireOp",EDGE,"E29");var subQ1=sQuery(id+"F4.wireOp",EDGE,"E27");var subQ2=makeQuery(id+"F4.imprint","INTERSECT",VERTEX,{"disambiguationData":[OD(0.0)],"derivedFrom":[subQ1,subQ0]});Q15=makeQuery(id+"F4.imprint","IMPRINT",FACE,{"disambiguationData":[TD([[makeQuery(id+"F4.imprint","IMPRINT",EDGE,{"disambiguationData":[TD([[subQ2,-1.0]])],"derivedFrom":subQ1}),1.0]])]});}
            var Q16;
            {var subQ0=sQuery(id+"F4.wireOp",EDGE,"E43");var subQ1=sQuery(id+"F4.wireOp",EDGE,"E27");var subQ2=makeQuery(id+"F4.imprint","INTERSECT",VERTEX,{"disambiguationData":[OD(0.0)],"derivedFrom":[subQ1,subQ0]});Q16=makeQuery(id+"F4.imprint","IMPRINT",FACE,{"disambiguationData":[TD([[makeQuery(id+"F4.imprint","IMPRINT",EDGE,{"disambiguationData":[TD([[subQ2,-1.0]])],"derivedFrom":subQ1}),-1.0]])]});}
            var Q17;
            {var subQ0=sQuery(id+"F4.wireOp",EDGE,"E43");var subQ1=sQuery(id+"F4.wireOp",EDGE,"E27");var subQ2=makeQuery(id+"F4.imprint","INTERSECT",VERTEX,{"disambiguationData":[OD(0.0)],"derivedFrom":[subQ1,subQ0]});Q17=makeQuery(id+"F4.imprint","IMPRINT",FACE,{"disambiguationData":[TD([[makeQuery(id+"F4.imprint","IMPRINT",EDGE,{"disambiguationData":[TD([[subQ2,-1.0]])],"derivedFrom":subQ1}),1.0]])]});}
            extrude(context, id + "F5", {"entities" : qUnion([Q0, Q1, Q2, Q3, Q4, Q5, Q6, Q7, Q8, Q9, Q10, Q11, Q12, Q13, Q14, Q15, Q16, Q17]), "operationType" : NewBodyOperationType.ADD, "depth" : 4 * mm});
        }
        {
            var Q0;
            Q0=makeQuery(id+"F5.opExtrude","CAP_EDGE",EDGE,{"disambiguationData":[OSD([sQuery(id+"F4.wireOp",EDGE,"E24.left")])],"isStart":false});
            var Q1;
            Q1=qBodyType(qCreatedBy(id+"FT8tyf5jn8AyVfC",EDGE),BodyType.WIRE);
            cPlane(context, id + "F6", {"entities" : qUnion([Q0, Q1]), "cplaneType" : CPlaneType.LINE_ANGLE, "offset" : 25 * mm, "angle" : 0 * degree, "width" : 150 * mm, "height" : 150 * mm});
        }
        {
            var Q0;
            Q0=qCreatedBy(id+"F6.planeOp",FACE);
            var sketch = newSketch(context, id + "F7", { "sketchPlane" : qUnion([Q0])});
            skLineSegment(sketch, "E48.bottom", {"start": v(0, 0) * mm, "end": v(-11.8, 0) * mm});
            skLineSegment(sketch, "E48.top", {"start": v(0, 31.9) * mm, "end": v(-11.8, 31.9) * mm});
            skLineSegment(sketch, "E48.left", {"start": v(0, 0) * mm, "end": v(0, 31.9) * mm});
            skLineSegment(sketch, "E48.right", {"start": v(-11.8, 0) * mm, "end": v(-11.8, 31.9) * mm});
            skLineSegment(sketch, "E49", {"start": v(-11.8, 27.2) * mm, "end": v(0, 27.2) * mm});
            skLineSegment(sketch, "E50", {"start": v(-11.8, 4.7) * mm, "end": v(0, 4.7) * mm});
            skLineSegment(sketch, "E51", {"start": v(-5.9, 31.9) * mm, "end": v(-5.9, 0) * mm});
            skCircle(sketch, "E52", {"center": v(-5.9, 21.3) * mm, "radius": 5.9 * mm});
            skPoint(sketch, "E52.first.point", {"position": v(-11.8, 21.3) * mm});
            skPoint(sketch, "E52.second.point", {"position": v(0, 21.3) * mm});
            skPoint(sketch, "E52.third.point", {"position": v(-5.9, 27.2) * mm});
            skCircle(sketch, "E53", {"center": v(-5.9, 21.3) * mm, "radius": 2.3 * mm});
            skPoint(sketch, "E54", {"position": v(-6.55, 31.9) * mm});
            skPoint(sketch, "E55", {"position": v(-5.25, 31.9) * mm});
            skPoint(sketch, "E56", {"position": v(-5.9, 29.6) * mm});
            skCircle(sketch, "E57", {"center": v(-5.9, 29.6) * mm, "radius": 1 * mm});
            skLineSegment(sketch, "E58", {"start": v(-6.55, 31.9) * mm, "end": v(-6.55, 30.36) * mm});
            skLineSegment(sketch, "E59", {"start": v(-5.25, 31.9) * mm, "end": v(-5.25, 30.36) * mm});
            skPoint(sketch, "E60", {"position": v(-11.8, 15.95) * mm});
            skPoint(sketch, "E61", {"position": v(0, 15.95) * mm});
            skLineSegment(sketch, "E62", {"start": v(-11.8, 15.95) * mm, "end": v(0, 15.95) * mm});
            skPoint(sketch, "E63.MirrorP", {"position": v(-5.9, 2.3) * mm});
            skLineSegment(sketch, "E64.MirrorCS", {"start": v(-6.55, 0) * mm, "end": v(-6.55, 1.54) * mm});
            skLineSegment(sketch, "E65.MirrorCS", {"start": v(-5.25, 0) * mm, "end": v(-5.25, 1.54) * mm});
            skCircle(sketch, "E66.MirrorC", {"center": v(-5.9, 2.3) * mm, "radius": 1 * mm});
            skCircle(sketch, "E67", {"center": v(-5.9, 21.3) * mm, "radius": 0.85 * mm});
            skPoint(sketch, "E68", {"position": v(-5.9, 12.5) * mm});
            skCircle(sketch, "E69", {"center": v(-5.9, 12.5) * mm, "radius": 2.5 * mm});
            skLineSegment(sketch, "E70", {"start": v(-3.4, 12.5) * mm, "end": v(-3.4, 15.96) * mm});
            skLineSegment(sketch, "E71", {"start": v(-8.4, 12.5) * mm, "end": v(-8.4, 15.96) * mm});
            skSolve(sketch);
        }
        {
            var Q0;
            {var subQ2=sQuery(id+"F7.wireOp",EDGE,"E51");var subQ5=sQuery(id+"F7.wireOp",EDGE,"E53");var subQ6=makeQuery(id+"F7.imprint","INTERSECT",VERTEX,{"disambiguationData":[OD(1.0)],"derivedFrom":[subQ2,subQ5]});Q0=makeQuery(id+"F7.imprint","IMPRINT",FACE,{"disambiguationData":[TD([[makeQuery(id+"F7.imprint","IMPRINT",EDGE,{"disambiguationData":[TD([[subQ6,-1.0]])],"derivedFrom":subQ2}),-1.0]])]});}
            var Q1;
            {var subQ5=sQuery(id+"F7.wireOp",EDGE,"E51");var subQ7=sQuery(id+"F7.wireOp",EDGE,"E53");var subQ8=makeQuery(id+"F7.imprint","INTERSECT",VERTEX,{"disambiguationData":[OD(1.0)],"derivedFrom":[subQ5,subQ7]});Q1=makeQuery(id+"F7.imprint","IMPRINT",FACE,{"disambiguationData":[TD([[makeQuery(id+"F7.imprint","IMPRINT",EDGE,{"disambiguationData":[TD([[subQ8,-1.0]])],"derivedFrom":subQ5}),1.0]])]});}
            var Q2;
            {var subQ0=sQuery(id+"F7.wireOp",EDGE,"E62");var subQ1=sQuery(id+"F7.wireOp",EDGE,"E51");var subQ2=makeQuery(id+"F7.imprint","INTERSECT",VERTEX,{"derivedFrom":[subQ1,subQ0]});Q2=makeQuery(id+"F7.imprint","IMPRINT",FACE,{"disambiguationData":[TD([[makeQuery(id+"F7.imprint","IMPRINT",EDGE,{"disambiguationData":[TD([[subQ2,-1.0]])],"derivedFrom":subQ1}),-1.0]])]});}
            var Q3;
            {var subQ0=sQuery(id+"F7.wireOp",EDGE,"E62");var subQ1=sQuery(id+"F7.wireOp",EDGE,"E51");var subQ2=makeQuery(id+"F7.imprint","INTERSECT",VERTEX,{"derivedFrom":[subQ1,subQ0]});Q3=makeQuery(id+"F7.imprint","IMPRINT",FACE,{"disambiguationData":[TD([[makeQuery(id+"F7.imprint","IMPRINT",EDGE,{"disambiguationData":[TD([[subQ2,-1.0]])],"derivedFrom":subQ1}),1.0]])]});}
            var Q4;
            {var subQ3=sQuery(id+"F7.wireOp",EDGE,"E51");var subQ6=sQuery(id+"F7.wireOp",EDGE,"E52");var subQ9=makeQuery(id+"F7.imprint","INTERSECT",VERTEX,{"derivedFrom":[subQ3,subQ6]});Q4=makeQuery(id+"F7.imprint","IMPRINT",FACE,{"disambiguationData":[TD([[makeQuery(id+"F7.imprint","IMPRINT",EDGE,{"disambiguationData":[TD([[subQ9,-1.0]])],"derivedFrom":subQ3}),-1.0]])]});}
            var Q5;
            {var subQ3=sQuery(id+"F7.wireOp",EDGE,"E51");var subQ6=sQuery(id+"F7.wireOp",EDGE,"E52");var subQ9=makeQuery(id+"F7.imprint","INTERSECT",VERTEX,{"derivedFrom":[subQ3,subQ6]});Q5=makeQuery(id+"F7.imprint","IMPRINT",FACE,{"disambiguationData":[TD([[makeQuery(id+"F7.imprint","IMPRINT",EDGE,{"disambiguationData":[TD([[subQ9,-1.0]])],"derivedFrom":subQ3}),1.0]])]});}
            var Q6;
            {var subQ0=sQuery(id+"F7.wireOp",EDGE,"E69");var subQ1=sQuery(id+"F7.wireOp",EDGE,"E51");var subQ2=makeQuery(id+"F7.imprint","INTERSECT",VERTEX,{"disambiguationData":[OD(0.0)],"derivedFrom":[subQ1,subQ0]});Q6=makeQuery(id+"F7.imprint","IMPRINT",FACE,{"disambiguationData":[TD([[makeQuery(id+"F7.imprint","IMPRINT",EDGE,{"disambiguationData":[TD([[subQ2,-1.0]])],"derivedFrom":subQ1}),-1.0]])]});}
            var Q7;
            {var subQ0=sQuery(id+"F7.wireOp",EDGE,"E69");var subQ1=sQuery(id+"F7.wireOp",EDGE,"E51");var subQ2=makeQuery(id+"F7.imprint","INTERSECT",VERTEX,{"disambiguationData":[OD(0.0)],"derivedFrom":[subQ1,subQ0]});Q7=makeQuery(id+"F7.imprint","IMPRINT",FACE,{"disambiguationData":[TD([[makeQuery(id+"F7.imprint","IMPRINT",EDGE,{"disambiguationData":[TD([[subQ2,-1.0]])],"derivedFrom":subQ1}),1.0]])]});}
            var Q8;
            {var subQ0=sQuery(id+"F7.wireOp",EDGE,"E53");var subQ1=sQuery(id+"F7.wireOp",EDGE,"E51");var subQ2=makeQuery(id+"F7.imprint","INTERSECT",VERTEX,{"disambiguationData":[OD(0.0)],"derivedFrom":[subQ1,subQ0]});Q8=makeQuery(id+"F7.imprint","IMPRINT",FACE,{"disambiguationData":[TD([[makeQuery(id+"F7.imprint","IMPRINT",EDGE,{"disambiguationData":[TD([[subQ2,-1.0]])],"derivedFrom":subQ1}),1.0]])]});}
            var Q9;
            {var subQ0=sQuery(id+"F7.wireOp",EDGE,"E53");var subQ1=sQuery(id+"F7.wireOp",EDGE,"E51");var subQ2=makeQuery(id+"F7.imprint","INTERSECT",VERTEX,{"disambiguationData":[OD(0.0)],"derivedFrom":[subQ1,subQ0]});Q9=makeQuery(id+"F7.imprint","IMPRINT",FACE,{"disambiguationData":[TD([[makeQuery(id+"F7.imprint","IMPRINT",EDGE,{"disambiguationData":[TD([[subQ2,-1.0]])],"derivedFrom":subQ1}),-1.0]])]});}
            var Q10;
            {var subQ0=sQuery(id+"F7.wireOp",EDGE,"E67");var subQ1=sQuery(id+"F7.wireOp",EDGE,"E51");var subQ2=makeQuery(id+"F7.imprint","INTERSECT",VERTEX,{"disambiguationData":[OD(0.0)],"derivedFrom":[subQ1,subQ0]});Q10=makeQuery(id+"F7.imprint","IMPRINT",FACE,{"disambiguationData":[TD([[makeQuery(id+"F7.imprint","IMPRINT",EDGE,{"disambiguationData":[TD([[subQ2,-1.0]])],"derivedFrom":subQ1}),-1.0]])]});}
            var Q11;
            {var subQ0=sQuery(id+"F7.wireOp",EDGE,"E67");var subQ1=sQuery(id+"F7.wireOp",EDGE,"E51");var subQ2=makeQuery(id+"F7.imprint","INTERSECT",VERTEX,{"disambiguationData":[OD(0.0)],"derivedFrom":[subQ1,subQ0]});Q11=makeQuery(id+"F7.imprint","IMPRINT",FACE,{"disambiguationData":[TD([[makeQuery(id+"F7.imprint","IMPRINT",EDGE,{"disambiguationData":[TD([[subQ2,-1.0]])],"derivedFrom":subQ1}),1.0]])]});}
            extrude(context, id + "F8", {"entities" : qUnion([Q0, Q1, Q2, Q3, Q4, Q5, Q6, Q7, Q8, Q9, Q10, Q11]), "operationType" : NewBodyOperationType.ADD, "depth" : 4 * mm});
        }
        {
            var Q0;
            Q0=makeQuery(id+"F8.opExtrude","CAP_FACE",FACE,{"disambiguationData":[OSD([sQuery(id+"F7.wireOp",EDGE,"E52"),sQuery(id+"F7.wireOp",EDGE,"E62"),sQuery(id+"F7.wireOp",EDGE,"E69"),sQuery(id+"F7.wireOp",EDGE,"E70"),sQuery(id+"F7.wireOp",EDGE,"E71")])],"isStart":false});
            cPlane(context, id + "F9", {"entities" : qUnion([Q0]), "cplaneType" : CPlaneType.OFFSET, "offset" : 0 * mm, "width" : 150 * mm, "height" : 150 * mm});
        }
        {
            var Q0;
            Q0=qCreatedBy(id+"F9.planeOp",FACE);
            var sketch = newSketch(context, id + "F10", { "sketchPlane" : qUnion([Q0])});
            skLineSegment(sketch, "E72.bottom", {"start": v(0, 0) * mm, "end": v(-11.8, 0) * mm});
            skLineSegment(sketch, "E72.top", {"start": v(0, 31.9) * mm, "end": v(-11.8, 31.9) * mm});
            skLineSegment(sketch, "E72.left", {"start": v(0, 0) * mm, "end": v(0, 31.9) * mm});
            skLineSegment(sketch, "E72.right", {"start": v(-11.8, 0) * mm, "end": v(-11.8, 31.9) * mm});
            skLineSegment(sketch, "E73", {"start": v(-11.8, 27.2) * mm, "end": v(0, 27.2) * mm});
            skLineSegment(sketch, "E74", {"start": v(-11.8, 4.7) * mm, "end": v(0, 4.7) * mm});
            skLineSegment(sketch, "E75", {"start": v(-5.9, 31.9) * mm, "end": v(-5.9, 0) * mm});
            skCircle(sketch, "E76", {"center": v(-5.9, 21.3) * mm, "radius": 5.9 * mm});
            skPoint(sketch, "E76.first.point", {"position": v(-11.8, 21.3) * mm});
            skPoint(sketch, "E76.second.point", {"position": v(0, 21.3) * mm});
            skPoint(sketch, "E76.third.point", {"position": v(-5.9, 27.2) * mm});
            skCircle(sketch, "E77", {"center": v(-5.9, 21.3) * mm, "radius": 4.3 * mm});
            skPoint(sketch, "E78", {"position": v(-6.55, 31.9) * mm});
            skPoint(sketch, "E79", {"position": v(-5.25, 31.9) * mm});
            skPoint(sketch, "E80", {"position": v(-5.9, 29.6) * mm});
            skCircle(sketch, "E81", {"center": v(-5.9, 29.6) * mm, "radius": 1 * mm});
            skLineSegment(sketch, "E82", {"start": v(-6.55, 31.9) * mm, "end": v(-6.55, 30.36) * mm});
            skLineSegment(sketch, "E83", {"start": v(-5.25, 31.9) * mm, "end": v(-5.25, 30.36) * mm});
            skPoint(sketch, "E84", {"position": v(-11.8, 15.95) * mm});
            skPoint(sketch, "E85", {"position": v(0, 15.95) * mm});
            skLineSegment(sketch, "E86", {"start": v(-11.8, 15.95) * mm, "end": v(0, 15.95) * mm});
            skPoint(sketch, "E87.MirrorP", {"position": v(-5.9, 2.3) * mm});
            skLineSegment(sketch, "E88.MirrorCS", {"start": v(-6.55, 0) * mm, "end": v(-6.55, 1.54) * mm});
            skLineSegment(sketch, "E89.MirrorCS", {"start": v(-5.25, 0) * mm, "end": v(-5.25, 1.54) * mm});
            skCircle(sketch, "E90.MirrorC", {"center": v(-5.9, 2.3) * mm, "radius": 1 * mm});
            skCircle(sketch, "E91", {"center": v(-5.9, 21.3) * mm, "radius": 0.85 * mm});
            skPoint(sketch, "E92", {"position": v(-5.9, 12.5) * mm});
            skCircle(sketch, "E93", {"center": v(-5.9, 12.5) * mm, "radius": 2.5 * mm});
            skLineSegment(sketch, "E94", {"start": v(-3.4, 12.5) * mm, "end": v(-3.4, 15.96) * mm});
            skLineSegment(sketch, "E95", {"start": v(-8.4, 12.5) * mm, "end": v(-8.4, 15.96) * mm});
            skSolve(sketch);
        }
        {
            var Q0;
            {var subQ0=sQuery(id+"F10.wireOp",EDGE,"E77");var subQ1=sQuery(id+"F10.wireOp",EDGE,"E75");var subQ2=makeQuery(id+"F10.imprint","INTERSECT",VERTEX,{"disambiguationData":[OD(0.0)],"derivedFrom":[subQ1,subQ0]});Q0=makeQuery(id+"F10.imprint","IMPRINT",FACE,{"disambiguationData":[TD([[makeQuery(id+"F10.imprint","IMPRINT",EDGE,{"disambiguationData":[TD([[subQ2,-1.0]])],"derivedFrom":subQ1}),-1.0]])]});}
            var Q1;
            {var subQ0=sQuery(id+"F10.wireOp",EDGE,"E77");var subQ1=sQuery(id+"F10.wireOp",EDGE,"E75");var subQ2=makeQuery(id+"F10.imprint","INTERSECT",VERTEX,{"disambiguationData":[OD(0.0)],"derivedFrom":[subQ1,subQ0]});Q1=makeQuery(id+"F10.imprint","IMPRINT",FACE,{"disambiguationData":[TD([[makeQuery(id+"F10.imprint","IMPRINT",EDGE,{"disambiguationData":[TD([[subQ2,-1.0]])],"derivedFrom":subQ1}),1.0]])]});}
            var Q2;
            {var subQ0=sQuery(id+"F10.wireOp",EDGE,"E91");var subQ1=sQuery(id+"F10.wireOp",EDGE,"E75");var subQ2=makeQuery(id+"F10.imprint","INTERSECT",VERTEX,{"disambiguationData":[OD(0.0)],"derivedFrom":[subQ1,subQ0]});Q2=makeQuery(id+"F10.imprint","IMPRINT",FACE,{"disambiguationData":[TD([[makeQuery(id+"F10.imprint","IMPRINT",EDGE,{"disambiguationData":[TD([[subQ2,-1.0]])],"derivedFrom":subQ1}),1.0]])]});}
            var Q3;
            {var subQ0=sQuery(id+"F10.wireOp",EDGE,"E91");var subQ1=sQuery(id+"F10.wireOp",EDGE,"E75");var subQ2=makeQuery(id+"F10.imprint","INTERSECT",VERTEX,{"disambiguationData":[OD(0.0)],"derivedFrom":[subQ1,subQ0]});Q3=makeQuery(id+"F10.imprint","IMPRINT",FACE,{"disambiguationData":[TD([[makeQuery(id+"F10.imprint","IMPRINT",EDGE,{"disambiguationData":[TD([[subQ2,-1.0]])],"derivedFrom":subQ1}),-1.0]])]});}
            extrude(context, id + "F11", {"entities" : qUnion([Q0, Q1, Q2, Q3]), "operationType" : NewBodyOperationType.ADD, "depth" : 3.2 * mm});
        }
        {
            var Q0;
            {var subQ0=sQuery(id+"F0.wireOp",EDGE,"E0.left");Q0=makeQuery(id+"F5.boolean.opBoolean","MERGE",FACE,{"derivedFrom":[makeQuery(id+"F2.boolean.opBoolean","MERGE",FACE,{"derivedFrom":[makeQuery(id+"F1.opExtrude","SWEPT_FACE",FACE,{"disambiguationData":[OSD([subQ0])]}),makeQuery(id+"F2.opExtrude","SWEPT_FACE",FACE,{"disambiguationData":[OSD([subQ0])]})]}),makeQuery(id+"F5.opExtrude","SWEPT_FACE",FACE,{"disambiguationData":[OSD([sQuery(id+"F4.wireOp",EDGE,"E24.left")])]})]});}
            var sketch = newSketch(context, id + "F12", { "sketchPlane" : qUnion([Q0])});
            skLineSegment(sketch, "E96", {"start": v(4.7, 2.5) * mm, "end": v(27.2, 2.5) * mm});
            skLineSegment(sketch, "E97", {"start": v(27.2, 2.5) * mm, "end": v(27.2, 0) * mm});
            skLineSegment(sketch, "E98", {"start": v(27.2, 0) * mm, "end": v(4.7, 0) * mm});
            skLineSegment(sketch, "E99", {"start": v(4.7, 0) * mm, "end": v(4.7, 2.5) * mm});
            skSolve(sketch);
        }
        {
            var Q0;
            Q0 = qSketchRegion(id + "F12", true);
            extrude(context, id + "F13", {"entities" : qUnion([Q0]), "operationType" : NewBodyOperationType.ADD, "depth" : 15 * mm, "offsetDistance" : 25 * mm});
        }
        {
            var Q0;
            {var subQ0=sQuery(id+"F0.wireOp",EDGE,"E0.right");Q0=makeQuery(id+"F5.boolean.opBoolean","MERGE",FACE,{"derivedFrom":[makeQuery(id+"F2.boolean.opBoolean","MERGE",FACE,{"derivedFrom":[makeQuery(id+"F1.opExtrude","SWEPT_FACE",FACE,{"disambiguationData":[OSD([subQ0])]}),makeQuery(id+"F2.opExtrude","SWEPT_FACE",FACE,{"disambiguationData":[OSD([subQ0])]})]}),makeQuery(id+"F5.opExtrude","SWEPT_FACE",FACE,{"disambiguationData":[OSD([sQuery(id+"F4.wireOp",EDGE,"E24.right")])]})]});}
            var sketch = newSketch(context, id + "F14", { "sketchPlane" : qUnion([Q0])});
            skLineSegment(sketch, "E100.bottom", {"start": v(-4.7, 2.5) * mm, "end": v(-27.2, 2.5) * mm});
            skLineSegment(sketch, "E100.top", {"start": v(-4.7, 0) * mm, "end": v(-27.2, 0) * mm});
            skLineSegment(sketch, "E100.left", {"start": v(-4.7, 2.5) * mm, "end": v(-4.7, 0) * mm});
            skLineSegment(sketch, "E100.right", {"start": v(-27.2, 2.5) * mm, "end": v(-27.2, 0) * mm});
            skSolve(sketch);
        }
        {
            var Q0;
            Q0 = qSketchRegion(id + "F14", true);
            extrude(context, id + "F15", {"entities" : qUnion([Q0]), "operationType" : NewBodyOperationType.ADD, "depth" : 15 * mm, "offsetDistance" : 25 * mm});
        }
    });
